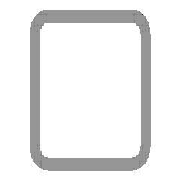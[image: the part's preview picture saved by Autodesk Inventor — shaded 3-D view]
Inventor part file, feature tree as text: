
AUTODESK INVENTOR PART (.ipt)
format: ipt  version: 2025.1 (Build 291241020, 241B)  size: 134,656 bytes
history: native  units: mm (DEFAULTED — no unit token found)
features: other x4, sketch x1, plane x1
ambient origin geometry x8: Origin, YZ Plane, XZ Plane, XY Plane, X Axis, Y Axis, Z Axis, Center Point
bodies: Solid1 (feature_tree), Body (feature_tree)
feature tree (6):
  parser-record x1  (decoder bookkeeping rows leaked as tree rows — omitted from the tree; the rows remain in map.json)
  other  "Driven Length"
  other  "Start Plane"
  other  "End Plane"
  sketch  "Sketch3"  dims[d3=1250.0mm d4=0.0mm d7=8.0mm d9=100.0mm d11=100.0mm d12=4.0mm d13=50.0mm d14=1300.0mm d15=50.0mm d16=50.0mm d17=90.0deg d18=1250.0mm]
  plane  "Work Plane3"
